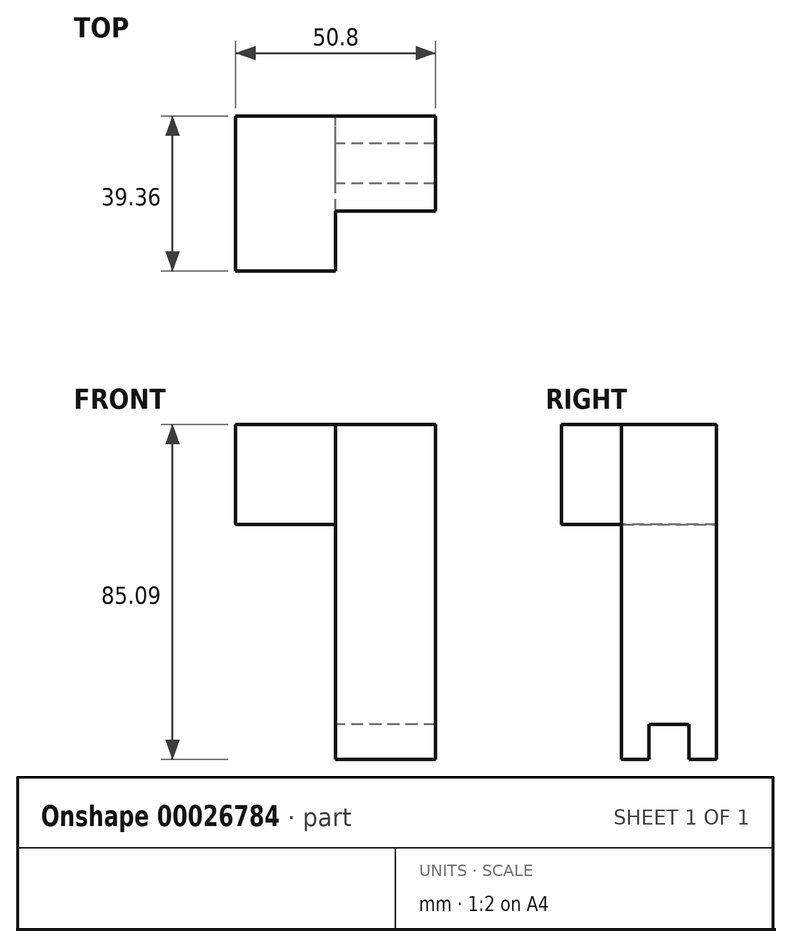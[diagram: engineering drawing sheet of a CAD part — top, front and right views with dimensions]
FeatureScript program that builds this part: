
annotation { "Feature Type Name" : "Feature", "Feature Type Description" : "" }
export const myFeature = defineFeature(function(context is Context, id is Id, definition is map)
    precondition{}
    {
        {
            var Q0;
            Q0=qCreatedBy(makeId("Top.planeOp"),FACE);
            var sketch = newSketch(context, id + "F0", { "sketchPlane" : qUnion([Q0])});
            skLineSegment(sketch, "E0.rect.bottom", {"start": v(12.7, -12.07) * mm, "end": v(-12.7, -12.07) * mm});
            skLineSegment(sketch, "E0.rect.top", {"start": v(12.7, 12.07) * mm, "end": v(-12.7, 12.07) * mm});
            skLineSegment(sketch, "E0.rect.left", {"start": v(12.7, -12.07) * mm, "end": v(12.7, 12.06) * mm});
            skLineSegment(sketch, "E0.rect.right", {"start": v(-12.7, -12.06) * mm, "end": v(-12.7, 12.07) * mm});
            skPoint(sketch, "E0.rect.middle", {"position": v(0, 0) * mm});
            skLineSegment(sketch, "E1.rect.bottom", {"start": v(12.7, -5.08) * mm, "end": v(-12.7, -5.08) * mm});
            skLineSegment(sketch, "E1.rect.top", {"start": v(12.7, 5.08) * mm, "end": v(-12.7, 5.08) * mm});
            skLineSegment(sketch, "E1.rect.left", {"start": v(12.7, -5.08) * mm, "end": v(12.7, 5.08) * mm});
            skLineSegment(sketch, "E1.rect.right", {"start": v(-12.7, -5.08) * mm, "end": v(-12.7, 5.08) * mm});
            skSolve(sketch);
        }
        {
            var Q0;
            Q0=qSketchRegion(id+"F0",true);
            extrude(context, id + "F1", {"entities" : qUnion([Q0]), "depth" : 50.8 * mm});
        }
        {
            var Q0;
            {var subQ2=sQuery(id+"F0.wireOp",EDGE,"E0.rect.bottom");Q0=makeQuery(id+"F0.imprint","IMPRINT",FACE,{"disambiguationData":[TD([[makeQuery(id+"F0.imprint","IMPRINT",EDGE,{"derivedFrom":subQ2}),-1.0]])]});}
            var Q1;
            {var subQ2=sQuery(id+"F0.wireOp",EDGE,"E0.rect.top");Q1=makeQuery(id+"F0.imprint","IMPRINT",FACE,{"disambiguationData":[TD([[makeQuery(id+"F0.imprint","IMPRINT",EDGE,{"derivedFrom":subQ2}),1.0]])]});}
            extrude(context, id + "F2", {"entities" : qUnion([Q0, Q1]), "operationType" : NewBodyOperationType.ADD, "oppositeDirection" : true, "depth" : 8.9 * mm});
        }
        {
            var Q0;
            Q0=makeQuery(id+"F1.opExtrude","CAP_FACE",FACE,{"disambiguationData":[OSD([sQuery(id+"F0.wireOp",EDGE,"E0.rect.bottom"),sQuery(id+"F0.wireOp",EDGE,"E0.rect.top"),sQuery(id+"F0.wireOp",EDGE,"E0.rect.left"),sQuery(id+"F0.wireOp",EDGE,"E0.rect.right"),sQuery(id+"F0.wireOp",EDGE,"E1.rect.left"),sQuery(id+"F0.wireOp",EDGE,"E1.rect.right")])],"isStart":false});
            var sketch = newSketch(context, id + "F3", { "sketchPlane" : qUnion([Q0])});
            skLineSegment(sketch, "E2.bottom", {"start": v(-12.7, 12.07) * mm, "end": v(12.7, 12.07) * mm});
            skLineSegment(sketch, "E2.top", {"start": v(-12.7, -12.07) * mm, "end": v(12.7, -12.07) * mm});
            skLineSegment(sketch, "E2.left", {"start": v(-12.7, 12.07) * mm, "end": v(-12.7, -12.07) * mm});
            skPoint(sketch, "E3.top.end.orphan", {"position": v(12.7, 35.22) * mm});
            skPoint(sketch, "E3.left.end.orphan", {"position": v(38.1, 35.22) * mm});
            skPoint(sketch, "E4.end.orphan", {"position": v(-12.7, 0) * mm});
            skPoint(sketch, "E4.start.orphan", {"position": v(38.1, 0) * mm});
            skLineSegment(sketch, "E5", {"start": v(0, -12.07) * mm, "end": v(0, 12.07) * mm});
            skLineSegment(sketch, "E6.MirrorCS", {"start": v(-38.1, 12.07) * mm, "end": v(-12.7, 12.07) * mm});
            skLineSegment(sketch, "E7.MirrorCS", {"start": v(-38.1, 12.07) * mm, "end": v(-38.1, -12.06) * mm});
            skLineSegment(sketch, "E8.MirrorCS", {"start": v(-38.1, -6.98) * mm, "end": v(-38.1, -27.3) * mm});
            skLineSegment(sketch, "E9.MirrorCS", {"start": v(-38.1, -27.3) * mm, "end": v(-12.7, -27.3) * mm});
            skLineSegment(sketch, "E10.MirrorCS", {"start": v(-12.7, -6.98) * mm, "end": v(-12.7, -27.3) * mm});
            skLineSegment(sketch, "E11", {"start": v(12.7, -12.07) * mm, "end": v(12.7, 12.07) * mm});
            skPoint(sketch, "E12.MirrorCS.end.orphan", {"position": v(12.7, -27.3) * mm});
            skPoint(sketch, "E12.MirrorCS.start.orphan", {"position": v(38.1, -27.3) * mm});
            skPoint(sketch, "E13.MirrorCS.end.orphan", {"position": v(12.7, -30.14) * mm});
            skPoint(sketch, "E13.MirrorCS.start.orphan", {"position": v(12.7, -6.98) * mm});
            skPoint(sketch, "E14.MirrorCS.end.orphan", {"position": v(38.1, -30.14) * mm});
            skPoint(sketch, "E14.MirrorCS.start.orphan", {"position": v(38.1, -6.98) * mm});
            skPoint(sketch, "E2.right.end.orphan", {"position": v(38.1, -12.07) * mm});
            skPoint(sketch, "E15.orphan", {"position": v(38.1, 12.07) * mm});
            skLineSegment(sketch, "E16", {"start": v(-38.1, -12.06) * mm, "end": v(-12.7, -12.07) * mm});
            skPoint(sketch, "E17.orphan", {"position": v(-38.1, -30.14) * mm});
            skPoint(sketch, "E18.orphan", {"position": v(-12.7, -30.14) * mm});
            skSolve(sketch);
        }
        {
            var Q0;
            Q0=qSketchRegion(id+"F3",true);
            extrude(context, id + "F4", {"entities" : qUnion([Q0]), "operationType" : NewBodyOperationType.ADD, "depth" : 25.4 * mm});
        }
    });
